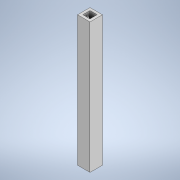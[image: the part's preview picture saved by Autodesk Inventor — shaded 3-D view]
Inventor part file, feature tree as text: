
AUTODESK INVENTOR PART (.ipt)
format: ipt  version: 2022 (Build 260153000, 153)  size: 111,104 bytes
history: native  units: mm
features: extrude x1, sketch x1
ambient origin geometry x8: Origin, YZ Plane, XZ Plane, XY Plane, X Axis, Y Axis, Z Axis, Center Point
bodies: Solid1 (feature_tree)
feature tree (2):
  extrude  "Extrusion1"  Depth=40.0mm
  sketch  "Sketch1"  dims[d0=190.0mm d1=40.0mm d2=40.0mm d3=110.0mm d4=40.0mm d5=110.0mm d6=190.0mm d7=40.0mm d8=31.0mm d9=28.0mm d10=2000.0mm d11=0.0mm]
